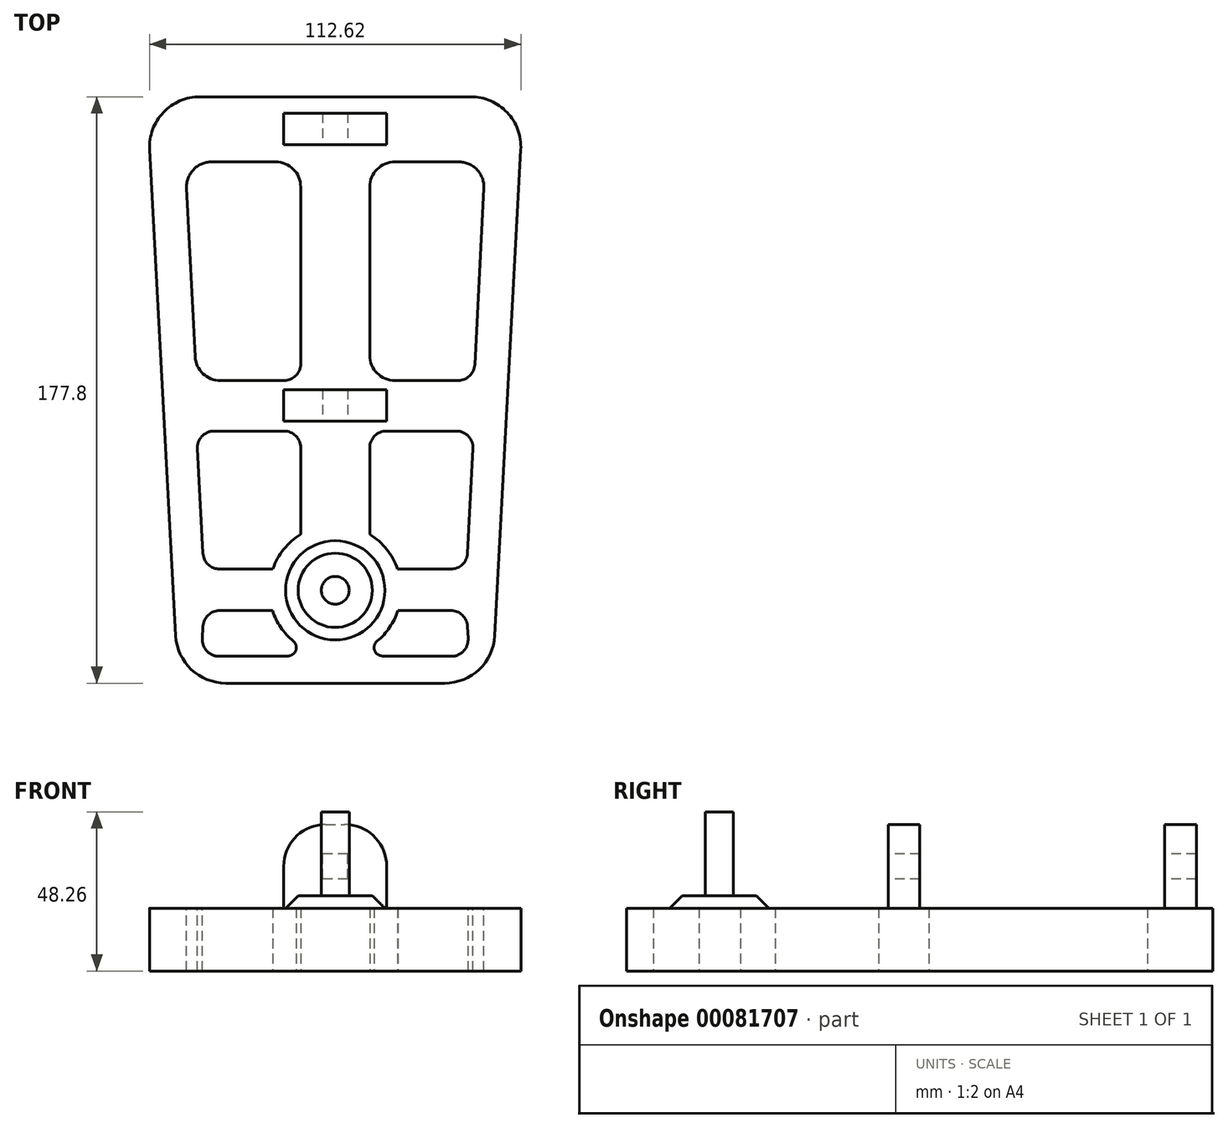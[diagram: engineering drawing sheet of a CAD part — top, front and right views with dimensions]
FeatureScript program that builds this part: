
annotation { "Feature Type Name" : "Feature", "Feature Type Description" : "" }
export const myFeature = defineFeature(function(context is Context, id is Id, definition is map)
    precondition{}
    {
        {
            var Q0;
            Q0=qCreatedBy(makeId("Top.planeOp"),FACE);
            var sketch = newSketch(context, id + "F0", { "sketchPlane" : qUnion([Q0])});
            skLineSegment(sketch, "E0", {"start": v(0, 90.84) * mm, "end": v(57.15, 90.84) * mm});
            skLineSegment(sketch, "E1", {"start": v(57.15, 90.84) * mm, "end": v(47.62, -86.96) * mm});
            skLineSegment(sketch, "E2", {"start": v(47.63, -86.96) * mm, "end": v(0, -86.96) * mm});
            skLineSegment(sketch, "E3.MirrorCS", {"start": v(0, 90.84) * mm, "end": v(-57.15, 90.84) * mm});
            skLineSegment(sketch, "E4.MirrorCS", {"start": v(-57.15, 90.84) * mm, "end": v(-47.63, -86.96) * mm});
            skLineSegment(sketch, "E5.MirrorCS", {"start": v(-47.63, -86.96) * mm, "end": v(0, -86.96) * mm});
            skLineSegment(sketch, "E6", {"start": v(10.47, 71.1) * mm, "end": v(45.5, 71.1) * mm});
            skLineSegment(sketch, "E7", {"start": v(45.5, 71.1) * mm, "end": v(42.1, 4.79) * mm});
            skLineSegment(sketch, "E8", {"start": v(42.1, 4.79) * mm, "end": v(10.47, 4.79) * mm});
            skLineSegment(sketch, "E9", {"start": v(10.47, 4.79) * mm, "end": v(10.47, 71.1) * mm});
            skLineSegment(sketch, "E10", {"start": v(42.1, -10.51) * mm, "end": v(39.85, -52.38) * mm});
            skLineSegment(sketch, "E11", {"start": v(39.85, -52.38) * mm, "end": v(18.9, -52.38) * mm});
            skLineSegment(sketch, "E12", {"start": v(10.47, -41.8) * mm, "end": v(10.47, -10.51) * mm});
            skLineSegment(sketch, "E13", {"start": v(10.47, -10.51) * mm, "end": v(42.1, -10.51) * mm});
            skLineSegment(sketch, "E14", {"start": v(39.85, -64.92) * mm, "end": v(40.6, -78.82) * mm});
            skLineSegment(sketch, "E15", {"start": v(40.6, -78.82) * mm, "end": v(10.47, -78.82) * mm});
            skLineSegment(sketch, "E16", {"start": v(10.47, -78.82) * mm, "end": v(10.47, -75.8) * mm});
            skLineSegment(sketch, "E17", {"start": v(19, -64.92) * mm, "end": v(39.85, -64.92) * mm});
            skArc(sketch, "E18", {"start": v(10.47, -75.8) * mm, "mid": v(15.71, -71.13) * mm, "end": v(19, -64.92) * mm});
            skPoint(sketch, "E19", {"position": v(18.9, -52.38) * mm});
            skPoint(sketch, "E20", {"position": v(18.9, -65.22) * mm});
            skArc(sketch, "E21.trimOffspring", {"start": v(18.9, -52.38) * mm, "mid": v(15.61, -46.35) * mm, "end": v(10.47, -41.8) * mm});
            skLineSegment(sketch, "E22.MirrorCS", {"start": v(-10.47, 4.79) * mm, "end": v(-10.47, 71.1) * mm});
            skLineSegment(sketch, "E23.MirrorCS", {"start": v(-10.47, 71.1) * mm, "end": v(-45.5, 71.1) * mm});
            skLineSegment(sketch, "E24.MirrorCS", {"start": v(-45.5, 71.1) * mm, "end": v(-42.1, 4.79) * mm});
            skLineSegment(sketch, "E25.MirrorCS", {"start": v(-42.1, 4.79) * mm, "end": v(-10.47, 4.79) * mm});
            skLineSegment(sketch, "E26.MirrorCS", {"start": v(-10.47, -10.51) * mm, "end": v(-42.1, -10.51) * mm});
            skLineSegment(sketch, "E27.MirrorCS", {"start": v(-10.47, -41.8) * mm, "end": v(-10.47, -10.51) * mm});
            skArc(sketch, "E28.MirrorCS", {"start": v(-18.9, -52.38) * mm, "mid": v(-15.61, -46.35) * mm, "end": v(-10.47, -41.8) * mm});
            skLineSegment(sketch, "E29.MirrorCS", {"start": v(-39.85, -52.38) * mm, "end": v(-18.9, -52.38) * mm});
            skLineSegment(sketch, "E30.MirrorCS", {"start": v(-42.1, -10.51) * mm, "end": v(-39.85, -52.38) * mm});
            skLineSegment(sketch, "E31.MirrorCS", {"start": v(-19, -64.92) * mm, "end": v(-39.85, -64.92) * mm});
            skArc(sketch, "E32.MirrorCS", {"start": v(-10.47, -75.8) * mm, "mid": v(-15.71, -71.13) * mm, "end": v(-19, -64.92) * mm});
            skLineSegment(sketch, "E33.MirrorCS", {"start": v(-40.6, -78.82) * mm, "end": v(-10.47, -78.82) * mm});
            skLineSegment(sketch, "E34.MirrorCS", {"start": v(-39.85, -64.92) * mm, "end": v(-40.6, -78.82) * mm});
            skLineSegment(sketch, "E35.MirrorCS", {"start": v(-10.47, -78.82) * mm, "end": v(-10.47, -75.8) * mm});
            skSolve(sketch);
        }
        {
            var Q0;
            Q0=makeQuery(id+"F0.imprint","IMPRINT",FACE,{"disambiguationData":[TD([[makeQuery(id+"F0.imprint","IMPRINT",EDGE,{"derivedFrom":sQuery(id+"F0.wireOp",EDGE,"E0")}),-1.0]])]});
            extrude(context, id + "F1", {"entities" : qUnion([Q0]), "depth" : 19.05 * mm});
        }
        {
            var Q0;
            Q0=makeQuery(id+"F1.opExtrude","CAP_FACE",FACE,{"disambiguationData":[OSD([sQuery(id+"F0.wireOp",EDGE,"E0"),sQuery(id+"F0.wireOp",EDGE,"E1"),sQuery(id+"F0.wireOp",EDGE,"E2"),sQuery(id+"F0.wireOp",EDGE,"E3.MirrorCS"),sQuery(id+"F0.wireOp",EDGE,"E4.MirrorCS"),sQuery(id+"F0.wireOp",EDGE,"E5.MirrorCS"),sQuery(id+"F0.wireOp",EDGE,"E6"),sQuery(id+"F0.wireOp",EDGE,"E7"),sQuery(id+"F0.wireOp",EDGE,"E8"),sQuery(id+"F0.wireOp",EDGE,"E9"),sQuery(id+"F0.wireOp",EDGE,"E10"),sQuery(id+"F0.wireOp",EDGE,"E11"),sQuery(id+"F0.wireOp",EDGE,"E12"),sQuery(id+"F0.wireOp",EDGE,"E13"),sQuery(id+"F0.wireOp",EDGE,"E14"),sQuery(id+"F0.wireOp",EDGE,"E15"),sQuery(id+"F0.wireOp",EDGE,"E16"),sQuery(id+"F0.wireOp",EDGE,"E17"),sQuery(id+"F0.wireOp",EDGE,"E18"),sQuery(id+"F0.wireOp",EDGE,"E21.trimOffspring"),sQuery(id+"F0.wireOp",EDGE,"E22.MirrorCS"),sQuery(id+"F0.wireOp",EDGE,"E23.MirrorCS"),sQuery(id+"F0.wireOp",EDGE,"E24.MirrorCS"),sQuery(id+"F0.wireOp",EDGE,"E25.MirrorCS"),sQuery(id+"F0.wireOp",EDGE,"E26.MirrorCS"),sQuery(id+"F0.wireOp",EDGE,"E27.MirrorCS"),sQuery(id+"F0.wireOp",EDGE,"E28.MirrorCS"),sQuery(id+"F0.wireOp",EDGE,"E29.MirrorCS"),sQuery(id+"F0.wireOp",EDGE,"E30.MirrorCS"),sQuery(id+"F0.wireOp",EDGE,"E31.MirrorCS"),sQuery(id+"F0.wireOp",EDGE,"E32.MirrorCS"),sQuery(id+"F0.wireOp",EDGE,"E33.MirrorCS"),sQuery(id+"F0.wireOp",EDGE,"E34.MirrorCS"),sQuery(id+"F0.wireOp",EDGE,"E35.MirrorCS")])],"isStart":false});
            var sketch = newSketch(context, id + "F2", { "sketchPlane" : qUnion([Q0])});
            skCircle(sketch, "E36", {"center": v(0, -58.8) * mm, "radius": 15.06 * mm});
            skSolve(sketch);
        }
        {
            var Q0;
            Q0=makeQuery(id+"F2.imprint","IMPRINT",FACE,{"disambiguationData":[TD([[makeQuery(id+"F2.imprint","IMPRINT",EDGE,{"derivedFrom":sQuery(id+"F2.wireOp",EDGE,"E36")}),1.0]])]});
            extrude(context, id + "F3", {"entities" : qUnion([Q0]), "operationType" : NewBodyOperationType.ADD, "depth" : 3.8 * mm});
        }
        {
            var Q0;
            Q0=makeQuery(id+"F3.opExtrude","CAP_FACE",FACE,{"disambiguationData":[OSD([sQuery(id+"F2.wireOp",EDGE,"E36")])],"isStart":false});
            var sketch = newSketch(context, id + "F4", { "sketchPlane" : qUnion([Q0])});
            skCircle(sketch, "E37", {"center": v(0, -58.8) * mm, "radius": 4.22 * mm});
            skSolve(sketch);
        }
        {
            var Q0;
            Q0=makeQuery(id+"F1.opExtrude","CAP_FACE",FACE,{"disambiguationData":[OSD([sQuery(id+"F0.wireOp",EDGE,"E0"),sQuery(id+"F0.wireOp",EDGE,"E1"),sQuery(id+"F0.wireOp",EDGE,"E2"),sQuery(id+"F0.wireOp",EDGE,"E3.MirrorCS"),sQuery(id+"F0.wireOp",EDGE,"E4.MirrorCS"),sQuery(id+"F0.wireOp",EDGE,"E5.MirrorCS"),sQuery(id+"F0.wireOp",EDGE,"E6"),sQuery(id+"F0.wireOp",EDGE,"E7"),sQuery(id+"F0.wireOp",EDGE,"E8"),sQuery(id+"F0.wireOp",EDGE,"E9"),sQuery(id+"F0.wireOp",EDGE,"E10"),sQuery(id+"F0.wireOp",EDGE,"E11"),sQuery(id+"F0.wireOp",EDGE,"E12"),sQuery(id+"F0.wireOp",EDGE,"E13"),sQuery(id+"F0.wireOp",EDGE,"E14"),sQuery(id+"F0.wireOp",EDGE,"E15"),sQuery(id+"F0.wireOp",EDGE,"E16"),sQuery(id+"F0.wireOp",EDGE,"E17"),sQuery(id+"F0.wireOp",EDGE,"E18"),sQuery(id+"F0.wireOp",EDGE,"E21.trimOffspring"),sQuery(id+"F0.wireOp",EDGE,"E22.MirrorCS"),sQuery(id+"F0.wireOp",EDGE,"E23.MirrorCS"),sQuery(id+"F0.wireOp",EDGE,"E24.MirrorCS"),sQuery(id+"F0.wireOp",EDGE,"E25.MirrorCS"),sQuery(id+"F0.wireOp",EDGE,"E26.MirrorCS"),sQuery(id+"F0.wireOp",EDGE,"E27.MirrorCS"),sQuery(id+"F0.wireOp",EDGE,"E28.MirrorCS"),sQuery(id+"F0.wireOp",EDGE,"E29.MirrorCS"),sQuery(id+"F0.wireOp",EDGE,"E30.MirrorCS"),sQuery(id+"F0.wireOp",EDGE,"E31.MirrorCS"),sQuery(id+"F0.wireOp",EDGE,"E32.MirrorCS"),sQuery(id+"F0.wireOp",EDGE,"E33.MirrorCS"),sQuery(id+"F0.wireOp",EDGE,"E34.MirrorCS"),sQuery(id+"F0.wireOp",EDGE,"E35.MirrorCS")])],"isStart":false});
            var sketch = newSketch(context, id + "F5", { "sketchPlane" : qUnion([Q0])});
            skLineSegment(sketch, "E38", {"start": v(0, 85.88) * mm, "end": v(15.61, 85.88) * mm});
            skLineSegment(sketch, "E39", {"start": v(15.61, 85.88) * mm, "end": v(15.61, 76.25) * mm});
            skLineSegment(sketch, "E40", {"start": v(15.61, 76.25) * mm, "end": v(0, 76.25) * mm});
            skLineSegment(sketch, "E41", {"start": v(0, -7.57) * mm, "end": v(15.61, -7.57) * mm});
            skLineSegment(sketch, "E42", {"start": v(15.61, -7.57) * mm, "end": v(15.61, 2.05) * mm});
            skLineSegment(sketch, "E43", {"start": v(15.61, 2.05) * mm, "end": v(0, 2.05) * mm});
            skLineSegment(sketch, "E44.MirrorCS", {"start": v(-15.61, 76.25) * mm, "end": v(0, 76.25) * mm});
            skLineSegment(sketch, "E45.MirrorCS", {"start": v(0, 85.88) * mm, "end": v(-15.61, 85.88) * mm});
            skLineSegment(sketch, "E46.MirrorCS", {"start": v(-15.61, 85.88) * mm, "end": v(-15.61, 76.25) * mm});
            skLineSegment(sketch, "E47.MirrorCS", {"start": v(-15.61, 2.05) * mm, "end": v(0, 2.05) * mm});
            skLineSegment(sketch, "E48.MirrorCS", {"start": v(0, -7.57) * mm, "end": v(-15.61, -7.57) * mm});
            skLineSegment(sketch, "E49.MirrorCS", {"start": v(-15.61, -7.57) * mm, "end": v(-15.61, 2.05) * mm});
            skSolve(sketch);
        }
        {
            var Q0;
            Q0=makeQuery(id+"F5.imprint","IMPRINT",FACE,{"disambiguationData":[TD([[makeQuery(id+"F5.imprint","IMPRINT",EDGE,{"derivedFrom":sQuery(id+"F5.wireOp",EDGE,"E38")}),-1.0]])]});
            var Q1;
            Q1=makeQuery(id+"F5.imprint","IMPRINT",FACE,{"disambiguationData":[TD([[makeQuery(id+"F5.imprint","IMPRINT",EDGE,{"derivedFrom":sQuery(id+"F5.wireOp",EDGE,"E41")}),1.0]])]});
            extrude(context, id + "F6", {"entities" : qUnion([Q0, Q1]), "operationType" : NewBodyOperationType.ADD, "depth" : 25.4 * mm});
        }
        {
            var Q0;
            Q0=makeQuery(id+"F6.opExtrude","SWEPT_FACE",FACE,{"disambiguationData":[OSD([sQuery(id+"F5.wireOp",EDGE,"E41"),sQuery(id+"F5.wireOp",EDGE,"E48.MirrorCS")])]});
            var sketch = newSketch(context, id + "F7", { "sketchPlane" : qUnion([Q0])});
            skLineSegment(sketch, "E50", {"start": v(0, 35.51) * mm, "end": v(3.81, 35.51) * mm});
            skLineSegment(sketch, "E51", {"start": v(3.81, 35.51) * mm, "end": v(3.81, 27.9) * mm});
            skLineSegment(sketch, "E52", {"start": v(3.81, 27.9) * mm, "end": v(0, 27.9) * mm});
            skLineSegment(sketch, "E53.MirrorCS", {"start": v(-3.81, 35.51) * mm, "end": v(-3.81, 27.9) * mm});
            skLineSegment(sketch, "E54.MirrorCS", {"start": v(-3.81, 27.9) * mm, "end": v(0, 27.9) * mm});
            skLineSegment(sketch, "E55.MirrorCS", {"start": v(0, 35.51) * mm, "end": v(-3.81, 35.51) * mm});
            skSolve(sketch);
        }
        {
            var Q0;
            Q0=makeQuery(id+"F7.imprint","IMPRINT",FACE,{"disambiguationData":[TD([[makeQuery(id+"F7.imprint","IMPRINT",EDGE,{"derivedFrom":sQuery(id+"F7.wireOp",EDGE,"E50")}),-1.0]])]});
            extrude(context, id + "F8", {"entities" : qUnion([Q0]), "operationType" : NewBodyOperationType.REMOVE, "endBound" : BoundingType.THROUGH_ALL, "oppositeDirection" : true, "depth" : 25.4 * mm});
        }
        {
            var Q0;
            Q0=makeQuery(id+"F4.imprint","IMPRINT",FACE,{"disambiguationData":[TD([[makeQuery(id+"F4.imprint","IMPRINT",EDGE,{"derivedFrom":sQuery(id+"F4.wireOp",EDGE,"E37")}),1.0]])]});
            extrude(context, id + "F9", {"entities" : qUnion([Q0]), "operationType" : NewBodyOperationType.ADD, "depth" : 25.4 * mm});
        }
        {
            var Q0;
            Q0=makeQuery(id+"F3.opExtrude","CAP_EDGE",EDGE,{"disambiguationData":[OSD([sQuery(id+"F2.wireOp",EDGE,"E36")])],"isStart":false});
            chamfer(context, id + "F10", {"entities" : qUnion([Q0]), "width" : 3.8 * mm, "tangentPropagation" : true});
        }
        {
            var Q0;
            Q0=makeQuery(id+"F6.opExtrude","CAP_EDGE",EDGE,{"disambiguationData":[OSD([sQuery(id+"F5.wireOp",EDGE,"E42")])],"isStart":false});
            var Q1;
            Q1=makeQuery(id+"F6.opExtrude","CAP_EDGE",EDGE,{"disambiguationData":[OSD([sQuery(id+"F5.wireOp",EDGE,"E49.MirrorCS")])],"isStart":false});
            fillet(context, id + "F11", {"entities" : qUnion([Q0, Q1]), "radius" : 12.7 * mm, "tangentPropagation" : true, "allowEdgeOverflow" : false});
        }
        {
            var Q0;
            Q0=makeQuery(id+"F6.opExtrude","CAP_EDGE",EDGE,{"disambiguationData":[OSD([sQuery(id+"F5.wireOp",EDGE,"E39")])],"isStart":false});
            var Q1;
            Q1=makeQuery(id+"F6.opExtrude","CAP_EDGE",EDGE,{"disambiguationData":[OSD([sQuery(id+"F5.wireOp",EDGE,"E46.MirrorCS")])],"isStart":false});
            fillet(context, id + "F12", {"entities" : qUnion([Q0, Q1]), "radius" : 12.7 * mm, "tangentPropagation" : true, "allowEdgeOverflow" : false});
        }
        {
            var Q0;
            Q0=makeQuery(id+"F1.opExtrude","SWEPT_EDGE",EDGE,{"disambiguationData":[OSD([sQuery(id+"F0.wireOp",EDGE,"E23.MirrorCS"),sQuery(id+"F0.wireOp",EDGE,"E24.MirrorCS")])]});
            fillet(context, id + "F13", {"entities" : qUnion([Q0]), "radius" : 7.62 * mm, "tangentPropagation" : true, "allowEdgeOverflow" : false});
        }
        {
            var Q0;
            Q0=makeQuery(id+"F1.opExtrude","SWEPT_EDGE",EDGE,{"disambiguationData":[OSD([sQuery(id+"F0.wireOp",EDGE,"E26.MirrorCS"),sQuery(id+"F0.wireOp",EDGE,"E30.MirrorCS")])]});
            fillet(context, id + "F14", {"entities" : qUnion([Q0]), "radius" : 5.08 * mm, "tangentPropagation" : true, "allowEdgeOverflow" : false});
        }
        {
            var Q0;
            Q0=makeQuery(id+"F1.opExtrude","SWEPT_EDGE",EDGE,{"disambiguationData":[OSD([sQuery(id+"F0.wireOp",EDGE,"E22.MirrorCS"),sQuery(id+"F0.wireOp",EDGE,"E23.MirrorCS")])]});
            var Q1;
            Q1=makeQuery(id+"F1.opExtrude","SWEPT_EDGE",EDGE,{"disambiguationData":[OSD([sQuery(id+"F0.wireOp",EDGE,"E6"),sQuery(id+"F0.wireOp",EDGE,"E7")])]});
            fillet(context, id + "F15", {"entities" : qUnion([Q0, Q1]), "radius" : 7.62 * mm, "tangentPropagation" : true, "allowEdgeOverflow" : false});
        }
        {
            var Q0;
            Q0=makeQuery(id+"F1.opExtrude","SWEPT_EDGE",EDGE,{"disambiguationData":[OSD([sQuery(id+"F0.wireOp",EDGE,"E24.MirrorCS"),sQuery(id+"F0.wireOp",EDGE,"E25.MirrorCS")])]});
            var Q1;
            Q1=makeQuery(id+"F1.opExtrude","SWEPT_EDGE",EDGE,{"disambiguationData":[OSD([sQuery(id+"F0.wireOp",EDGE,"E8"),sQuery(id+"F0.wireOp",EDGE,"E9")])]});
            fillet(context, id + "F16", {"entities" : qUnion([Q0, Q1]), "radius" : 7.62 * mm, "tangentPropagation" : true, "allowEdgeOverflow" : false});
        }
        {
            var Q0;
            Q0=makeQuery(id+"F1.opExtrude","SWEPT_EDGE",EDGE,{"disambiguationData":[OSD([sQuery(id+"F0.wireOp",EDGE,"E22.MirrorCS"),sQuery(id+"F0.wireOp",EDGE,"E25.MirrorCS")])]});
            var Q1;
            Q1=makeQuery(id+"F1.opExtrude","SWEPT_EDGE",EDGE,{"disambiguationData":[OSD([sQuery(id+"F0.wireOp",EDGE,"E7"),sQuery(id+"F0.wireOp",EDGE,"E8")])]});
            fillet(context, id + "F17", {"entities" : qUnion([Q0, Q1]), "radius" : 5.08 * mm, "tangentPropagation" : true, "allowEdgeOverflow" : false});
        }
        {
            var Q0;
            Q0=makeQuery(id+"F1.opExtrude","SWEPT_EDGE",EDGE,{"disambiguationData":[OSD([sQuery(id+"F0.wireOp",EDGE,"E6"),sQuery(id+"F0.wireOp",EDGE,"E9")])]});
            fillet(context, id + "F18", {"entities" : qUnion([Q0]), "radius" : 7.62 * mm, "tangentPropagation" : true, "allowEdgeOverflow" : false});
        }
        {
            var Q0;
            Q0=makeQuery(id+"F1.opExtrude","SWEPT_EDGE",EDGE,{"disambiguationData":[OSD([sQuery(id+"F0.wireOp",EDGE,"E26.MirrorCS"),sQuery(id+"F0.wireOp",EDGE,"E27.MirrorCS")])]});
            var Q1;
            Q1=makeQuery(id+"F1.opExtrude","SWEPT_EDGE",EDGE,{"disambiguationData":[OSD([sQuery(id+"F0.wireOp",EDGE,"E10"),sQuery(id+"F0.wireOp",EDGE,"E13")])]});
            var Q2;
            Q2=makeQuery(id+"F1.opExtrude","SWEPT_EDGE",EDGE,{"disambiguationData":[OSD([sQuery(id+"F0.wireOp",EDGE,"E12"),sQuery(id+"F0.wireOp",EDGE,"E13")])]});
            var Q3;
            Q3=makeQuery(id+"F1.opExtrude","SWEPT_EDGE",EDGE,{"disambiguationData":[OSD([sQuery(id+"F0.wireOp",EDGE,"E29.MirrorCS"),sQuery(id+"F0.wireOp",EDGE,"E30.MirrorCS")])]});
            var Q4;
            Q4=makeQuery(id+"F1.opExtrude","SWEPT_EDGE",EDGE,{"disambiguationData":[OSD([sQuery(id+"F0.wireOp",EDGE,"E10"),sQuery(id+"F0.wireOp",EDGE,"E11")])]});
            fillet(context, id + "F19", {"entities" : qUnion([Q0, Q1, Q2, Q3, Q4]), "radius" : 5.08 * mm, "tangentPropagation" : true, "allowEdgeOverflow" : false});
        }
        {
            var Q0;
            Q0=makeQuery(id+"F1.opExtrude","SWEPT_EDGE",EDGE,{"disambiguationData":[OSD([sQuery(id+"F0.wireOp",EDGE,"E14"),sQuery(id+"F0.wireOp",EDGE,"E15")])]});
            var Q1;
            Q1=makeQuery(id+"F1.opExtrude","SWEPT_EDGE",EDGE,{"disambiguationData":[OSD([sQuery(id+"F0.wireOp",EDGE,"E33.MirrorCS"),sQuery(id+"F0.wireOp",EDGE,"E35.MirrorCS")])]});
            var Q2;
            Q2=makeQuery(id+"F1.opExtrude","SWEPT_EDGE",EDGE,{"disambiguationData":[OSD([sQuery(id+"F0.wireOp",EDGE,"E33.MirrorCS"),sQuery(id+"F0.wireOp",EDGE,"E34.MirrorCS")])]});
            var Q3;
            Q3=makeQuery(id+"F1.opExtrude","SWEPT_EDGE",EDGE,{"disambiguationData":[OSD([sQuery(id+"F0.wireOp",EDGE,"E15"),sQuery(id+"F0.wireOp",EDGE,"E16")])]});
            var Q4;
            Q4=makeQuery(id+"F1.opExtrude","SWEPT_EDGE",EDGE,{"disambiguationData":[OSD([sQuery(id+"F0.wireOp",EDGE,"E14"),sQuery(id+"F0.wireOp",EDGE,"E17")])]});
            var Q5;
            Q5=makeQuery(id+"F1.opExtrude","SWEPT_EDGE",EDGE,{"disambiguationData":[OSD([sQuery(id+"F0.wireOp",EDGE,"E31.MirrorCS"),sQuery(id+"F0.wireOp",EDGE,"E34.MirrorCS")])]});
            fillet(context, id + "F20", {"entities" : qUnion([Q0, Q1, Q2, Q3, Q4, Q5]), "radius" : 5.08 * mm, "tangentPropagation" : true, "allowEdgeOverflow" : false});
        }
        {
            var Q0;
            Q0=makeQuery(id+"F20.opFillet","BLEND_EDGE",EDGE,{"blendedFrom":[makeQuery(id+"F1.opExtrude","SWEPT_EDGE",EDGE,{"disambiguationData":[OSD([sQuery(id+"F0.wireOp",EDGE,"E15"),sQuery(id+"F0.wireOp",EDGE,"E16")])]}),makeQuery(id+"F1.opExtrude","SWEPT_FACE",FACE,{"disambiguationData":[OSD([sQuery(id+"F0.wireOp",EDGE,"E18")])]})],"blendedInto":[makeQuery(id+"F1.opExtrude","SWEPT_FACE",FACE,{"disambiguationData":[OSD([sQuery(id+"F0.wireOp",EDGE,"E18")])]})]});
            var Q1;
            Q1=makeQuery(id+"F20.opFillet","BLEND_EDGE",EDGE,{"blendedFrom":[makeQuery(id+"F1.opExtrude","SWEPT_EDGE",EDGE,{"disambiguationData":[OSD([sQuery(id+"F0.wireOp",EDGE,"E33.MirrorCS"),sQuery(id+"F0.wireOp",EDGE,"E35.MirrorCS")])]}),makeQuery(id+"F1.opExtrude","SWEPT_FACE",FACE,{"disambiguationData":[OSD([sQuery(id+"F0.wireOp",EDGE,"E32.MirrorCS")])]})],"blendedInto":[makeQuery(id+"F1.opExtrude","SWEPT_FACE",FACE,{"disambiguationData":[OSD([sQuery(id+"F0.wireOp",EDGE,"E32.MirrorCS")])]})]});
            fillet(context, id + "F21", {"entities" : qUnion([Q0, Q1]), "radius" : 2.54 * mm, "tangentPropagation" : true, "allowEdgeOverflow" : false});
        }
        {
            var Q0;
            Q0=makeQuery(id+"F1.opExtrude","SWEPT_EDGE",EDGE,{"disambiguationData":[OSD([sQuery(id+"F0.wireOp",EDGE,"E4.MirrorCS"),sQuery(id+"F0.wireOp",EDGE,"E5.MirrorCS")])]});
            var Q1;
            Q1=makeQuery(id+"F1.opExtrude","SWEPT_EDGE",EDGE,{"disambiguationData":[OSD([sQuery(id+"F0.wireOp",EDGE,"E3.MirrorCS"),sQuery(id+"F0.wireOp",EDGE,"E4.MirrorCS")])]});
            var Q2;
            Q2=makeQuery(id+"F1.opExtrude","SWEPT_EDGE",EDGE,{"disambiguationData":[OSD([sQuery(id+"F0.wireOp",EDGE,"E0"),sQuery(id+"F0.wireOp",EDGE,"E1")])]});
            var Q3;
            Q3=makeQuery(id+"F1.opExtrude","SWEPT_EDGE",EDGE,{"disambiguationData":[OSD([sQuery(id+"F0.wireOp",EDGE,"E1"),sQuery(id+"F0.wireOp",EDGE,"E2")])]});
            fillet(context, id + "F22", {"entities" : qUnion([Q0, Q1, Q2, Q3]), "radius" : 15.24 * mm, "tangentPropagation" : true, "allowEdgeOverflow" : false});
        }
    });
